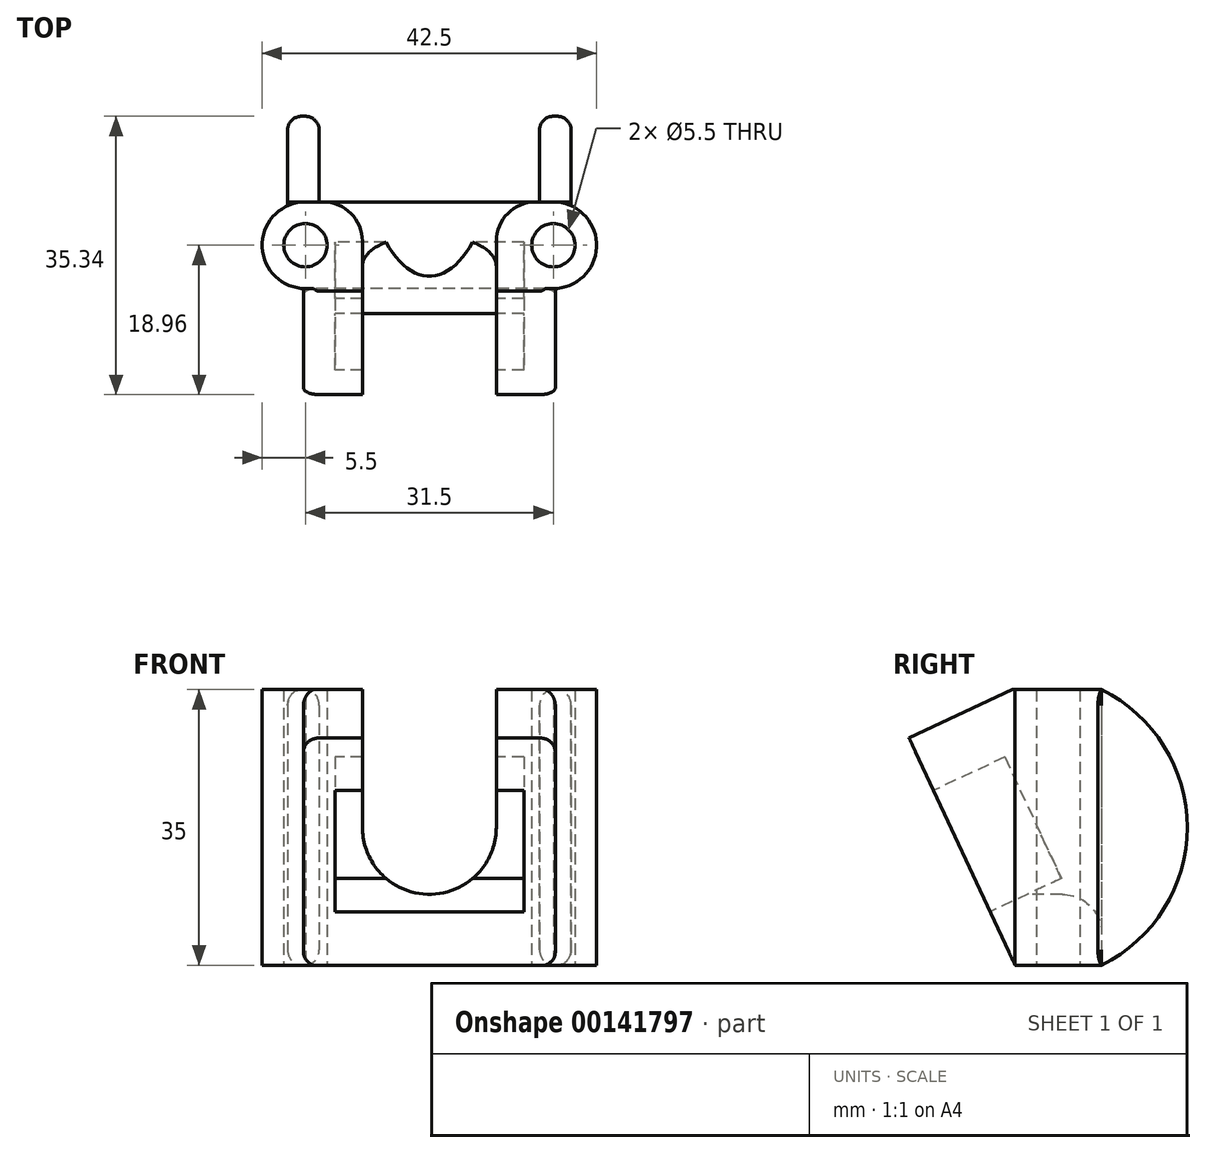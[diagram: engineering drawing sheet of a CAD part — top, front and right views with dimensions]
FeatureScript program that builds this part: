
annotation { "Feature Type Name" : "Feature", "Feature Type Description" : "" }
export const myFeature = defineFeature(function(context is Context, id is Id, definition is map)
    precondition{}
    {
        {
            var Q0;
            Q0=qCreatedBy(makeId("Top.planeOp"),FACE);
            var sketch = newSketch(context, id + "F0", { "sketchPlane" : qUnion([Q0])});
            skLineSegment(sketch, "E0", {"start": v(-18.5, 0) * mm, "end": v(18.5, 0) * mm, "construction": true});
            skCircle(sketch, "E1", {"center": v(-15.75, 0) * mm, "radius": 2.75 * mm});
            skCircle(sketch, "E2", {"center": v(15.75, 0) * mm, "radius": 2.75 * mm});
            skArc(sketch, "E3", {"start": v(-15.75, 5.5) * mm, "mid": v(-21.25, 0) * mm, "end": v(-15.75, -5.5) * mm});
            skArc(sketch, "E4", {"start": v(15.75, -5.5) * mm, "mid": v(21.25, 0) * mm, "end": v(15.75, 5.5) * mm});
            skLineSegment(sketch, "E5", {"start": v(-15.75, 5.5) * mm, "end": v(15.75, 5.5) * mm});
            skLineSegment(sketch, "E6", {"start": v(-15.75, -5.5) * mm, "end": v(15.75, -5.5) * mm});
            skSolve(sketch);
        }
        {
            var Q0;
            Q0=makeQuery(id+"F0.imprint","IMPRINT",FACE,{"disambiguationData":[TD([[makeQuery(id+"F0.imprint","IMPRINT",EDGE,{"derivedFrom":sQuery(id+"F0.wireOp",EDGE,"E1")}),-1.0]])]});
            extrude(context, id + "F1", {"entities" : qUnion([Q0]), "depth" : 35 * mm});
        }
        {
            var Q0;
            Q0=makeQuery(id+"F1.opExtrude","SWEPT_FACE",FACE,{"disambiguationData":[OSD([sQuery(id+"F0.wireOp",EDGE,"E6")])]});
            var sketch = newSketch(context, id + "F2", { "sketchPlane" : qUnion([Q0])});
            skLineSegment(sketch, "E7", {"start": v(-15.75, 35) * mm, "end": v(15.75, 0) * mm, "construction": true});
            skArc(sketch, "E8", {"start": v(-8.5, 17.5) * mm, "mid": v(0, 9) * mm, "end": v(8.5, 17.5) * mm});
            skLineSegment(sketch, "E9", {"start": v(-8.5, 17.5) * mm, "end": v(-8.5, 35) * mm});
            skLineSegment(sketch, "E10", {"start": v(8.5, 17.5) * mm, "end": v(8.5, 35) * mm});
            skLineSegment(sketch, "E11", {"start": v(8.5, 35) * mm, "end": v(-8.5, 35) * mm});
            skSolve(sketch);
        }
        {
            var Q0;
            Q0=qSketchRegion(id+"F2",true);
            extrude(context, id + "F3", {"entities" : qUnion([Q0]), "operationType" : NewBodyOperationType.REMOVE, "endBound" : BoundingType.THROUGH_ALL, "oppositeDirection" : true, "depth" : 25 * mm});
        }
        {
            var Q0;
            Q0=makeQuery(id+"F1.opExtrude","CAP_EDGE",EDGE,{"disambiguationData":[OSD([sQuery(id+"F0.wireOp",EDGE,"E6")])],"isStart":true});
            cPlane(context, id + "F4", {"entities" : qUnion([Q0]), "cplaneType" : CPlaneType.LINE_ANGLE, "offset" : 150 * mm, "angle" : 25 * degree, "width" : 150 * mm, "height" : 150 * mm});
        }
        {
            var Q0;
            Q0=qCreatedBy(id+"F4.planeOp",FACE);
            var sketch = newSketch(context, id + "F5", { "sketchPlane" : qUnion([Q0])});
            skPoint(sketch, "E12.0", {"position": v(15.75, 2.32) * mm});
            skPoint(sketch, "E13.0", {"position": v(-15.75, 34.05) * mm});
            skLineSegment(sketch, "E14", {"start": v(-15.75, 34.05) * mm, "end": v(15.75, 2.32) * mm, "construction": true});
            skLineSegment(sketch, "E15.rect.bottom", {"start": v(14, 32.18) * mm, "end": v(-14, 32.18) * mm, "construction": true});
            skLineSegment(sketch, "E15.rect.top", {"start": v(14, 4.18) * mm, "end": v(-14, 4.18) * mm, "construction": true});
            skLineSegment(sketch, "E15.rect.left", {"start": v(14, 32.18) * mm, "end": v(14, 4.18) * mm, "construction": true});
            skLineSegment(sketch, "E15.rect.right", {"start": v(-14, 32.18) * mm, "end": v(-14, 4.18) * mm, "construction": true});
            skPoint(sketch, "E15.rect.middle", {"position": v(0, 18.18) * mm});
            skLineSegment(sketch, "E16.0", {"start": v(14, 34.18) * mm, "end": v(-14, 34.18) * mm});
            skLineSegment(sketch, "E16.1", {"start": v(16, 32.18) * mm, "end": v(16, 4.18) * mm});
            skLineSegment(sketch, "E16.2", {"start": v(14, 2.18) * mm, "end": v(-14, 2.18) * mm});
            skLineSegment(sketch, "E16.3", {"start": v(-16, 32.18) * mm, "end": v(-16, 4.18) * mm});
            skPoint(sketch, "E17.visualSharp", {"position": v(16, 34.18) * mm});
            skArc(sketch, "E17.filletArc", {"start": v(16, 32.18) * mm, "mid": v(15.41, 33.6) * mm, "end": v(14, 34.18) * mm});
            skPoint(sketch, "E18.visualSharp", {"position": v(16, 2.18) * mm});
            skArc(sketch, "E18.filletArc", {"start": v(14, 2.18) * mm, "mid": v(15.41, 2.77) * mm, "end": v(16, 4.18) * mm});
            skPoint(sketch, "E19.visualSharp", {"position": v(-16, 2.18) * mm});
            skArc(sketch, "E19.filletArc", {"start": v(-16, 4.18) * mm, "mid": v(-15.41, 2.77) * mm, "end": v(-14, 2.18) * mm});
            skPoint(sketch, "E20.visualSharp", {"position": v(-16, 34.18) * mm});
            skArc(sketch, "E20.filletArc", {"start": v(-14, 34.18) * mm, "mid": v(-15.41, 33.6) * mm, "end": v(-16, 32.18) * mm});
            skSolve(sketch);
        }
        {
            var Q0;
            Q0=makeQuery(id+"F5.imprint","IMPRINT",FACE,{"disambiguationData":[TD([[makeQuery(id+"F5.imprint","IMPRINT",EDGE,{"derivedFrom":sQuery(id+"F5.wireOp",EDGE,"E16.0")}),1.0]])]});
            var Q1;
            Q1=makeQuery(id+"F1.opExtrude","SWEPT_FACE",FACE,{"disambiguationData":[OSD([sQuery(id+"F0.wireOp",EDGE,"E6")])]});
            extrude(context, id + "F6", {"entities" : qUnion([Q0]), "operationType" : NewBodyOperationType.ADD, "endBound" : BoundingType.UP_TO_SURFACE, "endBoundEntityFace" : qUnion([Q1]), "depth" : 25 * mm});
        }
        {
            var Q0;
            Q0=makeQuery(id+"F1.opExtrude","SWEPT_FACE",FACE,{"disambiguationData":[OSD([sQuery(id+"F0.wireOp",EDGE,"E5")])]});
            var sketch = newSketch(context, id + "F7", { "sketchPlane" : qUnion([Q0])});
            skLineSegment(sketch, "E21.0", {"start": v(-8.5, 35) * mm, "end": v(-8.5, 17.5) * mm});
            skLineSegment(sketch, "E22.0", {"start": v(8.5, 35) * mm, "end": v(8.5, 17.5) * mm});
            skArc(sketch, "E23.0", {"start": v(-8.5, 17.5) * mm, "mid": v(0, 9) * mm, "end": v(8.5, 17.5) * mm});
            skLineSegment(sketch, "E24", {"start": v(-8.5, 35) * mm, "end": v(8.5, 35) * mm});
            skLineSegment(sketch, "E25.bottom", {"start": v(15.75, 35) * mm, "end": v(-15.75, 35) * mm});
            skLineSegment(sketch, "E25.top", {"start": v(15.75, 35.6) * mm, "end": v(-15.75, 35.6) * mm});
            skLineSegment(sketch, "E25.left", {"start": v(15.75, 35) * mm, "end": v(15.75, 35.6) * mm});
            skLineSegment(sketch, "E25.right", {"start": v(-15.75, 35) * mm, "end": v(-15.75, 35.6) * mm});
            skSolve(sketch);
        }
        {
            var Q0;
            Q0=qSketchRegion(id+"F7",true);
            extrude(context, id + "F8", {"entities" : qUnion([Q0]), "operationType" : NewBodyOperationType.REMOVE, "oppositeDirection" : true, "depth" : 25 * mm});
        }
        {
            var Q0;
            Q0=makeQuery(id+"F6.opExtrude","CAP_FACE",FACE,{"disambiguationData":[OSD([sQuery(id+"F5.wireOp",EDGE,"E16.0"),sQuery(id+"F5.wireOp",EDGE,"E16.1"),sQuery(id+"F5.wireOp",EDGE,"E16.2"),sQuery(id+"F5.wireOp",EDGE,"E16.3"),sQuery(id+"F5.wireOp",EDGE,"E17.filletArc"),sQuery(id+"F5.wireOp",EDGE,"E18.filletArc"),sQuery(id+"F5.wireOp",EDGE,"E19.filletArc"),sQuery(id+"F5.wireOp",EDGE,"E20.filletArc")])],"isStart":true});
            var sketch = newSketch(context, id + "F9", { "sketchPlane" : qUnion([Q0])});
            skLineSegment(sketch, "E26", {"start": v(-13, 31.33) * mm, "end": v(13, 5.33) * mm, "construction": true});
            skLineSegment(sketch, "E27.rect.bottom", {"start": v(12, 26.83) * mm, "end": v(-12, 26.83) * mm});
            skLineSegment(sketch, "E27.rect.top", {"start": v(12, 9.83) * mm, "end": v(-12, 9.83) * mm});
            skLineSegment(sketch, "E27.rect.left", {"start": v(12, 26.83) * mm, "end": v(12, 9.83) * mm});
            skLineSegment(sketch, "E27.rect.right", {"start": v(-12, 26.83) * mm, "end": v(-12, 9.83) * mm});
            skPoint(sketch, "E27.rect.middle", {"position": v(0, 18.33) * mm});
            skSolve(sketch);
        }
        {
            var Q0;
            {var subQ1=makeQuery(id+"F6.opExtrude","CAP_FACE",FACE,{"disambiguationData":[OSD([sQuery(id+"F5.wireOp",EDGE,"E16.0"),sQuery(id+"F5.wireOp",EDGE,"E16.1"),sQuery(id+"F5.wireOp",EDGE,"E16.2"),sQuery(id+"F5.wireOp",EDGE,"E16.3"),sQuery(id+"F5.wireOp",EDGE,"E17.filletArc"),sQuery(id+"F5.wireOp",EDGE,"E18.filletArc"),sQuery(id+"F5.wireOp",EDGE,"E19.filletArc"),sQuery(id+"F5.wireOp",EDGE,"E20.filletArc")])],"isStart":true});var subQ6=makeQuery(id+"F8.boolean.opBoolean","INTERSECT",EDGE,{"derivedFrom":[subQ1,makeQuery(id+"F8.opExtrude","SWEPT_FACE",FACE,{"disambiguationData":[OSD([sQuery(id+"F7.wireOp",EDGE,"E23.0")])]})]});Q0=makeQuery(id+"F9.imprint","IMPRINT",FACE,{"disambiguationData":[TD([[makeQuery(id+"F9.imprint","IMPRINT",EDGE,{"derivedFrom":subQ6}),-1.0]])]});}
            var Q1;
            Q1=makeQuery(id+"F9.imprint","IMPRINT",FACE,{"disambiguationData":[TD([[makeQuery(id+"F9.imprint","IMPRINT",EDGE,{"derivedFrom":sQuery(id+"F9.wireOp",EDGE,"E27.rect.top")}),-1.0]])]});
            extrude(context, id + "F10", {"entities" : qUnion([Q0, Q1]), "operationType" : NewBodyOperationType.REMOVE, "oppositeDirection" : true, "depth" : 10 * mm});
        }
        {
            var Q0;
            Q0=makeQuery(id+"F6.opExtrude","SWEPT_FACE",FACE,{"disambiguationData":[OSD([sQuery(id+"F5.wireOp",EDGE,"E16.3")])]});
            var sketch = newSketch(context, id + "F11", { "sketchPlane" : qUnion([Q0])});
            skPoint(sketch, "E28.0", {"position": v(5.5, 35) * mm});
            skPoint(sketch, "E29.0", {"position": v(5.5, 0) * mm});
            skLineSegment(sketch, "E30.0", {"start": v(5.5, 35) * mm, "end": v(5.5, 0) * mm});
            skArc(sketch, "E31", {"start": v(5.5, 0) * mm, "mid": v(16.38, 17.5) * mm, "end": v(5.5, 35) * mm});
            skSolve(sketch);
        }
        {
            var Q0;
            Q0=makeQuery(id+"F11.imprint","IMPRINT",FACE,{"disambiguationData":[TD([[makeQuery(id+"F11.imprint","IMPRINT",EDGE,{"derivedFrom":sQuery(id+"F11.wireOp",EDGE,"E30.0")}),1.0]])]});
            extrude(context, id + "F12", {"entities" : qUnion([Q0]), "operationType" : NewBodyOperationType.ADD, "depth" : 2 * mm, "hasSecondDirection" : true, "secondDirectionOppositeDirection" : true, "secondDirectionDepth" : 2 * mm});
        }
        {
            var Q0;
            Q0=makeQuery(id+"F1.opExtrude","SWEPT_BODY",BODY,{"disambiguationData":[OSD([sQuery(id+"F0.wireOp",EDGE,"E1"),sQuery(id+"F0.wireOp",EDGE,"E2"),sQuery(id+"F0.wireOp",EDGE,"E3"),sQuery(id+"F0.wireOp",EDGE,"E4"),sQuery(id+"F0.wireOp",EDGE,"E5"),sQuery(id+"F0.wireOp",EDGE,"E6")])]});
            var Q1;
            Q1=qCreatedBy(makeId("Right.planeOp"),FACE);
            mirror(context, id + "F13", {"operationType" : NewBodyOperationType.ADD, "entities" : qUnion([Q0]), "mirrorPlane" : qUnion([Q1])});
        }
        {
            var Q0;
            Q0=makeQuery(id+"F12.opExtrude","CAP_EDGE",EDGE,{"disambiguationData":[OSD([sQuery(id+"F11.wireOp",EDGE,"E31")])],"isStart":false});
            var Q1;
            Q1=makeQuery(id+"F12.opExtrude","CAP_EDGE",EDGE,{"disambiguationData":[OSD([sQuery(id+"F11.wireOp",EDGE,"E31")])],"isStart":true});
            var Q2;
            Q2=makeQuery(id+"F13.opPattern","COPY",EDGE,{"derivedFrom":makeQuery(id+"F12.opExtrude","CAP_EDGE",EDGE,{"disambiguationData":[OSD([sQuery(id+"F11.wireOp",EDGE,"E31")])],"isStart":true}),"instanceName":"1"});
            var Q3;
            Q3=makeQuery(id+"F13.opPattern","COPY",EDGE,{"derivedFrom":makeQuery(id+"F12.opExtrude","CAP_EDGE",EDGE,{"disambiguationData":[OSD([sQuery(id+"F11.wireOp",EDGE,"E31")])],"isStart":false}),"instanceName":"1"});
            fillet(context, id + "F14", {"entities" : qUnion([Q0, Q1, Q2, Q3]), "radius" : 1.75 * mm, "tangentPropagation" : true, "allowEdgeOverflow" : false});
        }
        {
            var Q0;
            Q0=makeQuery(id+"F3.boolean.opBoolean","INTERSECT",EDGE,{"derivedFrom":[makeQuery(id+"F1.opExtrude","SWEPT_FACE",FACE,{"disambiguationData":[OSD([sQuery(id+"F0.wireOp",EDGE,"E5")])]}),makeQuery(id+"F3.opExtrude","SWEPT_FACE",FACE,{"disambiguationData":[OSD([sQuery(id+"F2.wireOp",EDGE,"E10")])]})]});
            fillet(context, id + "F15", {"entities" : qUnion([Q0]), "radius" : 5 * mm, "tangentPropagation" : true, "allowEdgeOverflow" : false});
        }
        {
            var Q0;
            Q0=makeQuery(id+"F12.opExtrude","SWEPT_FACE",FACE,{"disambiguationData":[OSD([sQuery(id+"F11.wireOp",EDGE,"E30.0")])]});
            var Q1;
            Q1=makeQuery(id+"F1.opExtrude","SWEPT_FACE",FACE,{"disambiguationData":[OSD([sQuery(id+"F0.wireOp",EDGE,"E4")])]});
            extrude(context, id + "F16", {"entities" : qUnion([Q0]), "operationType" : NewBodyOperationType.ADD, "endBound" : BoundingType.UP_TO_SURFACE, "endBoundEntityFace" : qUnion([Q1]), "depth" : 25 * mm});
        }
        {
            var Q0;
            Q0=makeQuery(id+"F13.opPattern","COPY",FACE,{"derivedFrom":makeQuery(id+"F12.opExtrude","SWEPT_FACE",FACE,{"disambiguationData":[OSD([sQuery(id+"F11.wireOp",EDGE,"E30.0")])]}),"instanceName":"1"});
            var Q1;
            Q1=makeQuery(id+"F1.opExtrude","SWEPT_FACE",FACE,{"disambiguationData":[OSD([sQuery(id+"F0.wireOp",EDGE,"E3")])]});
            extrude(context, id + "F17", {"entities" : qUnion([Q0]), "operationType" : NewBodyOperationType.ADD, "endBound" : BoundingType.UP_TO_SURFACE, "endBoundEntityFace" : qUnion([Q1]), "depth" : 25 * mm});
        }
    });
